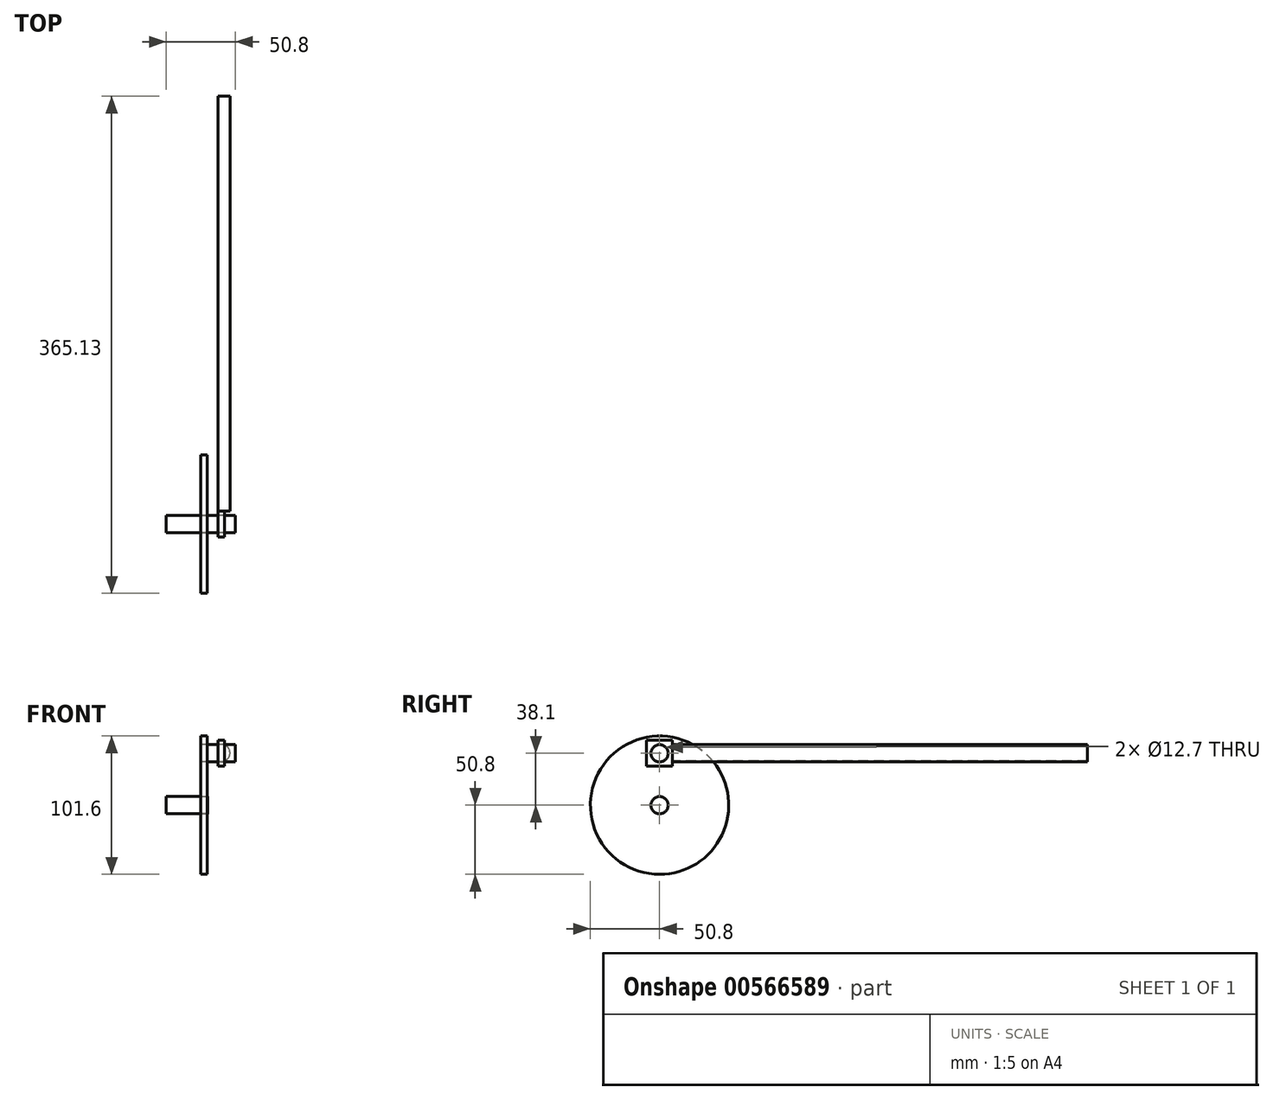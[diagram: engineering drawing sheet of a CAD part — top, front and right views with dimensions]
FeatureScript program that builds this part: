
annotation { "Feature Type Name" : "Feature", "Feature Type Description" : "" }
export const myFeature = defineFeature(function(context is Context, id is Id, definition is map)
    precondition{}
    {
        {
            var Q0;
            Q0=qCreatedBy(makeId("Right.planeOp"),FACE);
            var sketch = newSketch(context, id + "F0", { "sketchPlane" : qUnion([Q0])});
            skCircle(sketch, "E0", {"center": v(0, 0) * mm, "radius": 50.8 * mm});
            skCircle(sketch, "E1", {"center": v(0, 38.1) * mm, "radius": 6.35 * mm});
            skCircle(sketch, "E2", {"center": v(0, 0) * mm, "radius": 6.35 * mm});
            skSolve(sketch);
        }
        {
            var Q0;
            {var subQ1=sQuery(id+"F0.wireOp",EDGE,"E0");var subQ3=sQuery(id+"F0.wireOp",EDGE,"nnnFxugn-CSQ3-aM5i-BOC8-MykUcugMUkDe");var subQ5=makeQuery(id+"F0.imprint","INTERSECT",VERTEX,{"disambiguationData":[OD(0.0)],"derivedFrom":[subQ1,subQ3]});Q0=makeQuery(id+"F0.imprint","IMPRINT",FACE,{"disambiguationData":[TD([[makeQuery(id+"F0.imprint","IMPRINT",EDGE,{"disambiguationData":[TD([[subQ5,-1.0]])],"derivedFrom":subQ1}),1.0]])]});}
            var Q1;
            {var subQ1=sQuery(id+"F0.wireOp",EDGE,"nnnFxugn-CSQ3-aM5i-BOC8-MykUcugMUkDe");var subQ5=sQuery(id+"F0.wireOp",EDGE,"E0");var subQ7=makeQuery(id+"F0.imprint","INTERSECT",VERTEX,{"disambiguationData":[OD(0.0)],"derivedFrom":[subQ5,subQ1]});Q1=makeQuery(id+"F0.imprint","IMPRINT",FACE,{"disambiguationData":[TD([[makeQuery(id+"F0.imprint","IMPRINT",EDGE,{"disambiguationData":[TD([[subQ7,1.0]])],"derivedFrom":subQ5}),1.0]])]});}
            var Q2;
            {var subQ0=sQuery(id+"F0.wireOp",EDGE,"nnnFxugn-CSQ3-aM5i-BOC8-MykUcugMUkDe");var subQ1=sQuery(id+"F0.wireOp",EDGE,"E0");var subQ2=makeQuery(id+"F0.imprint","INTERSECT",VERTEX,{"disambiguationData":[OD(1.0)],"derivedFrom":[subQ1,subQ0]});Q2=makeQuery(id+"F0.imprint","IMPRINT",FACE,{"disambiguationData":[TD([[makeQuery(id+"F0.imprint","IMPRINT",EDGE,{"disambiguationData":[TD([[subQ2,-1.0]])],"derivedFrom":subQ1}),1.0]])]});}
            var Q3;
            {var subQ0=sQuery(id+"F0.wireOp",EDGE,"nnnFxugn-CSQ3-aM5i-BOC8-MykUcugMUkDe");var subQ1=sQuery(id+"F0.wireOp",EDGE,"E0");var subQ2=makeQuery(id+"F0.imprint","INTERSECT",VERTEX,{"disambiguationData":[OD(1.0)],"derivedFrom":[subQ1,subQ0]});Q3=makeQuery(id+"F0.imprint","IMPRINT",FACE,{"disambiguationData":[TD([[makeQuery(id+"F0.imprint","IMPRINT",EDGE,{"disambiguationData":[TD([[subQ2,1.0]])],"derivedFrom":subQ1}),1.0]])]});}
            var Q4;
            {var subQ0=sQuery(id+"F0.wireOp",EDGE,"E1");var subQ1=sQuery(id+"F0.wireOp",EDGE,"nnnFxugn-CSQ3-aM5i-BOC8-MykUcugMUkDe");var subQ2=makeQuery(id+"F0.imprint","INTERSECT",VERTEX,{"disambiguationData":[OD(0.0)],"derivedFrom":[subQ1,subQ0]});Q4=makeQuery(id+"F0.imprint","IMPRINT",FACE,{"disambiguationData":[TD([[makeQuery(id+"F0.imprint","IMPRINT",EDGE,{"disambiguationData":[TD([[subQ2,-1.0]])],"derivedFrom":subQ1}),1.0]])]});}
            var Q5;
            {var subQ0=sQuery(id+"F0.wireOp",EDGE,"E1");var subQ1=sQuery(id+"F0.wireOp",EDGE,"nnnFxugn-CSQ3-aM5i-BOC8-MykUcugMUkDe");var subQ2=makeQuery(id+"F0.imprint","INTERSECT",VERTEX,{"disambiguationData":[OD(0.0)],"derivedFrom":[subQ1,subQ0]});Q5=makeQuery(id+"F0.imprint","IMPRINT",FACE,{"disambiguationData":[TD([[makeQuery(id+"F0.imprint","IMPRINT",EDGE,{"disambiguationData":[TD([[subQ2,-1.0]])],"derivedFrom":subQ1}),-1.0]])]});}
            var Q6;
            Q6=makeQuery(id+"F0.imprint","IMPRINT",FACE,{"disambiguationData":[TD([[makeQuery(id+"F0.imprint","IMPRINT",EDGE,{"derivedFrom":sQuery(id+"F0.wireOp",EDGE,"E0")}),1.0]])]});
            extrude(context, id + "F1", {"entities" : qUnion([Q0, Q1, Q2, Q3, Q4, Q5, Q6]), "depth" : 4.76 * mm, "offsetDistance" : 25.4 * mm});
        }
        {
            var Q0;
            Q0=makeQuery(id+"F0.imprint","IMPRINT",FACE,{"disambiguationData":[TD([[makeQuery(id+"F0.imprint","IMPRINT",EDGE,{"derivedFrom":sQuery(id+"F0.wireOp",EDGE,"E1")}),1.0]])]});
            extrude(context, id + "F2", {"entities" : qUnion([Q0]), "depth" : 25.4 * mm, "offsetDistance" : 25.4 * mm});
        }
        {
            var Q0;
            Q0=makeQuery(id+"F2.opExtrude","CAP_FACE",FACE,{"disambiguationData":[OSD([sQuery(id+"F0.wireOp",EDGE,"E1")])],"isStart":false});
            cPlane(context, id + "F3", {"entities" : qUnion([Q0]), "cplaneType" : CPlaneType.OFFSET, "offset" : 12.7 * mm, "oppositeDirection" : true, "width" : 152.4 * mm, "height" : 152.4 * mm});
        }
        {
            var Q0;
            Q0=qCreatedBy(id+"F3.planeOp",FACE);
            var sketch = newSketch(context, id + "F4", { "sketchPlane" : qUnion([Q0])});
            skLineSegment(sketch, "E3.bottom", {"start": v(9.52, 47.8) * mm, "end": v(-9.53, 47.8) * mm});
            skLineSegment(sketch, "E3.top", {"start": v(9.52, 28.76) * mm, "end": v(-9.53, 28.76) * mm});
            skLineSegment(sketch, "E3.left", {"start": v(9.52, 47.8) * mm, "end": v(9.52, 28.76) * mm});
            skLineSegment(sketch, "E3.right", {"start": v(-9.53, 47.8) * mm, "end": v(-9.53, 28.76) * mm});
            skPoint(sketch, "E3.middle", {"position": v(0, 38.28) * mm});
            skSolve(sketch);
        }
        {
            var Q0;
            Q0=makeQuery(id+"F4.imprint","IMPRINT",FACE,{"disambiguationData":[TD([[makeQuery(id+"F4.imprint","IMPRINT",EDGE,{"derivedFrom":sQuery(id+"F4.wireOp",EDGE,"E3.bottom")}),1.0]])]});
            extrude(context, id + "F5", {"entities" : qUnion([Q0]), "depth" : 4.76 * mm, "offsetDistance" : 25.4 * mm});
        }
        {
            var Q0;
            Q0=makeQuery(id+"F5.opExtrude","SWEPT_FACE",FACE,{"disambiguationData":[OSD([sQuery(id+"F4.wireOp",EDGE,"E3.left")])]});
            var sketch = newSketch(context, id + "F6", { "sketchPlane" : qUnion([Q0])});
            skCircle(sketch, "E4", {"center": v(-15.08, 38.28) * mm, "radius": 6.35 * mm});
            skSolve(sketch);
        }
        {
            var Q0;
            {var subQ0=sQuery(id+"F6.wireOp",EDGE,"E4");var subQ1=makeQuery(id+"F5.opExtrude","CAP_EDGE",EDGE,{"disambiguationData":[OSD([sQuery(id+"F4.wireOp",EDGE,"E3.left")])],"isStart":false});var subQ2=makeQuery(id+"F6.imprint","INTERSECT",VERTEX,{"disambiguationData":[OD(0.0)],"derivedFrom":[subQ1,subQ0]});Q0=makeQuery(id+"F6.imprint","IMPRINT",FACE,{"disambiguationData":[TD([[makeQuery(id+"F6.imprint","IMPRINT",EDGE,{"disambiguationData":[TD([[subQ2,-1.0]])],"derivedFrom":subQ0}),1.0]])]});}
            var Q1;
            {var subQ0=sQuery(id+"F6.wireOp",EDGE,"E4");var subQ1=sQuery(id+"F4.wireOp",EDGE,"E3.left");var subQ2=makeQuery(id+"F5.opExtrude","CAP_EDGE",EDGE,{"disambiguationData":[OSD([subQ1])],"isStart":false});var subQ3=makeQuery(id+"F6.imprint","INTERSECT",VERTEX,{"disambiguationData":[OD(0.0)],"derivedFrom":[subQ2,subQ0]});Q1=makeQuery(id+"F6.imprint","IMPRINT",FACE,{"disambiguationData":[TD([[makeQuery(id+"F6.imprint","IMPRINT",EDGE,{"disambiguationData":[TD([[subQ3,1.0]])],"derivedFrom":subQ0}),1.0]])]});}
            var Q2;
            {var subQ0=sQuery(id+"F6.wireOp",EDGE,"E4");var subQ1=makeQuery(id+"F5.opExtrude","CAP_EDGE",EDGE,{"disambiguationData":[OSD([sQuery(id+"F4.wireOp",EDGE,"E3.left")])],"isStart":true});var subQ2=makeQuery(id+"F6.imprint","INTERSECT",VERTEX,{"disambiguationData":[OD(0.0)],"derivedFrom":[subQ1,subQ0]});Q2=makeQuery(id+"F6.imprint","IMPRINT",FACE,{"disambiguationData":[TD([[makeQuery(id+"F6.imprint","IMPRINT",EDGE,{"disambiguationData":[TD([[subQ2,1.0]])],"derivedFrom":subQ0}),1.0]])]});}
            extrude(context, id + "F7", {"entities" : qUnion([Q0, Q1, Q2]), "operationType" : NewBodyOperationType.ADD, "depth" : 304.8 * mm, "offsetDistance" : 25.4 * mm});
        }
        {
            var Q0;
            Q0=makeQuery(id+"F0.imprint","IMPRINT",FACE,{"disambiguationData":[TD([[makeQuery(id+"F0.imprint","IMPRINT",EDGE,{"derivedFrom":sQuery(id+"F0.wireOp",EDGE,"E2")}),1.0]])]});
            extrude(context, id + "F8", {"entities" : qUnion([Q0]), "oppositeDirection" : true, "depth" : 25.4 * mm, "offsetDistance" : 25.4 * mm, "hasSecondDirection" : true, "secondDirectionOppositeDirection" : false, "secondDirectionDepth" : 5.08 * mm});
        }
    });
